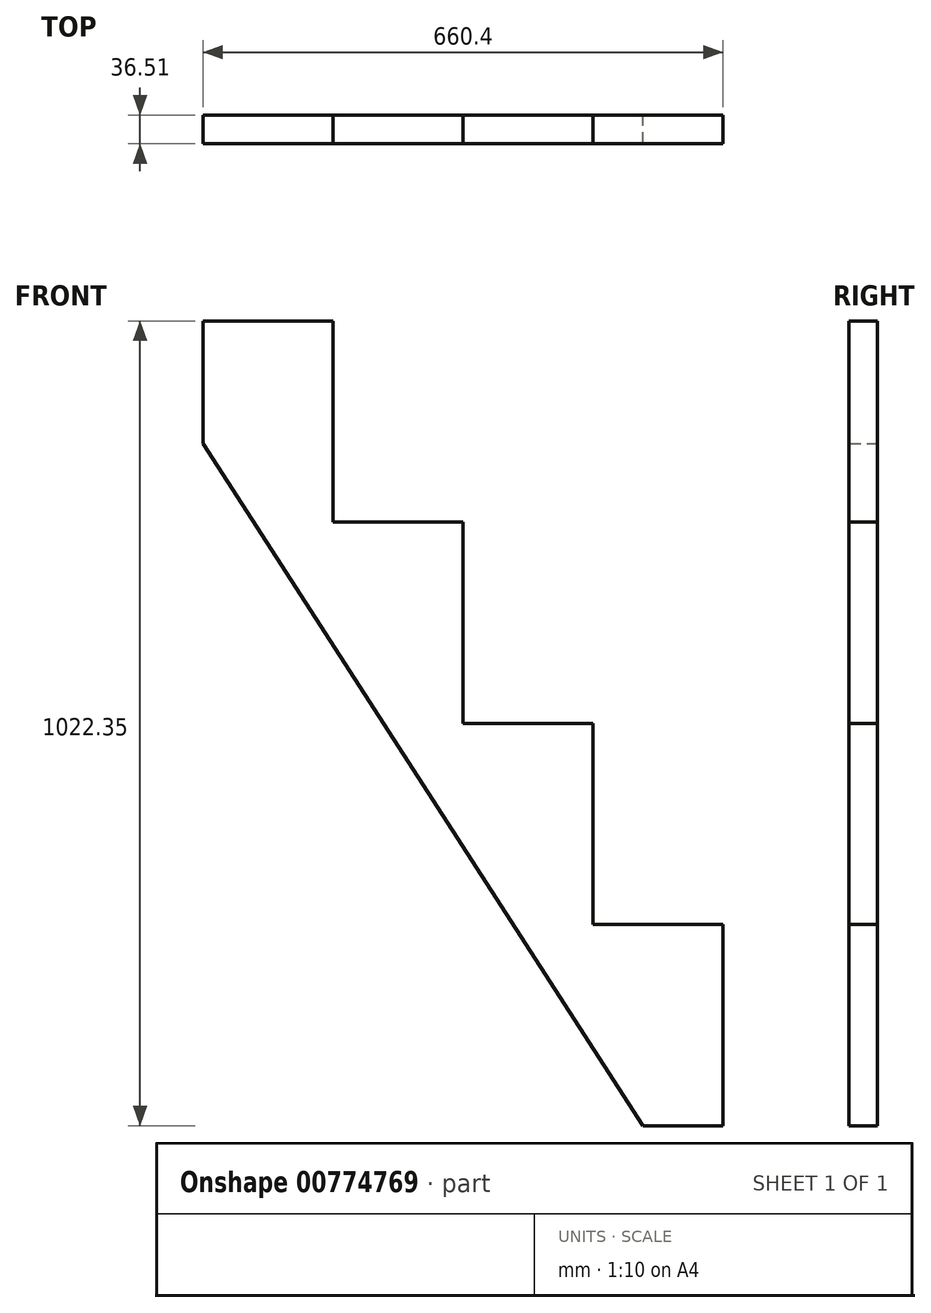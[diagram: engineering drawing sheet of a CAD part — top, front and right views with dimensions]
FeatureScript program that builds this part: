
annotation { "Feature Type Name" : "Feature", "Feature Type Description" : "" }
export const myFeature = defineFeature(function(context is Context, id is Id, definition is map)
    precondition{}
    {
        {
            var Q0;
            Q0=qCreatedBy(makeId("Front.planeOp"),FACE);
            var sketch = newSketch(context, id + "F0", { "sketchPlane" : qUnion([Q0])});
            skLineSegment(sketch, "E0.top", {"start": v(0, 255.59) * mm, "end": v(-165.1, 255.59) * mm});
            skLineSegment(sketch, "E0.left", {"start": v(0, 0) * mm, "end": v(0, 255.59) * mm});
            skLineSegment(sketch, "E0.right", {"start": v(-165.1, 100.01) * mm, "end": v(-165.1, 255.59) * mm});
            skLineSegment(sketch, "E1.bottom", {"start": v(0, 0) * mm, "end": v(165.1, 0) * mm});
            skLineSegment(sketch, "E1.right", {"start": v(165.1, 0) * mm, "end": v(165.1, -255.59) * mm});
            skLineSegment(sketch, "E2.bottom", {"start": v(165.1, -255.59) * mm, "end": v(330.2, -255.59) * mm});
            skLineSegment(sketch, "E2.right", {"start": v(330.2, -255.59) * mm, "end": v(330.2, -511.17) * mm});
            skLineSegment(sketch, "E3.bottom", {"start": v(330.2, -511.17) * mm, "end": v(495.3, -511.17) * mm});
            skLineSegment(sketch, "E3.right", {"start": v(495.3, -511.17) * mm, "end": v(495.3, -766.76) * mm});
            skLineSegment(sketch, "E4", {"start": v(495.3, -766.76) * mm, "end": v(393.7, -766.76) * mm});
            skLineSegment(sketch, "E5", {"start": v(-165.1, 100.01) * mm, "end": v(393.7, -766.76) * mm});
            skSolve(sketch);
        }
        {
            var Q0;
            Q0 = qSketchRegion(id + "F0", true);
            extrude(context, id + "F1", {"entities" : qUnion([Q0]), "depth" : 36.5 * mm, "offsetDistance" : 25.4 * mm});
        }
    });
